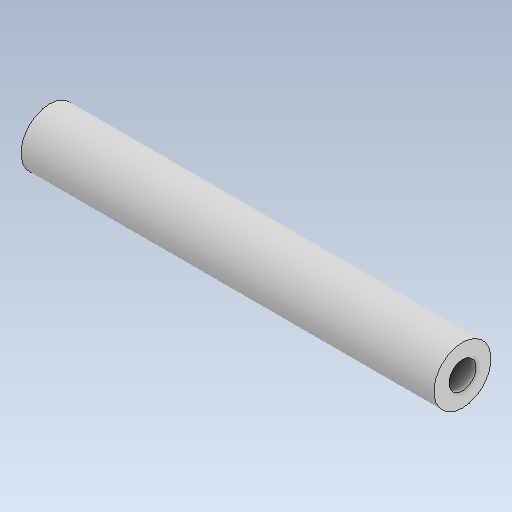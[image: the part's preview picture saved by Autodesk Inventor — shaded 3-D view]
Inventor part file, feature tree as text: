
AUTODESK INVENTOR PART (.ipt)
format: ipt  version: 2020 (Build 240168000, 168)  size: 93,184 bytes
history: native  units: mm
features: other x1, extrude x1, sketch x1
ambient origin geometry x8: Origin, YZ Plane, XZ Plane, XY Plane, X Axis, Y Axis, Z Axis, Center Point
bodies: Body1 (feature_tree)
feature tree (3):
  other  "Твердое тело1"
  extrude  "Выдавливание1"  Depth=3.3mm
  sketch  "Эскиз1"
